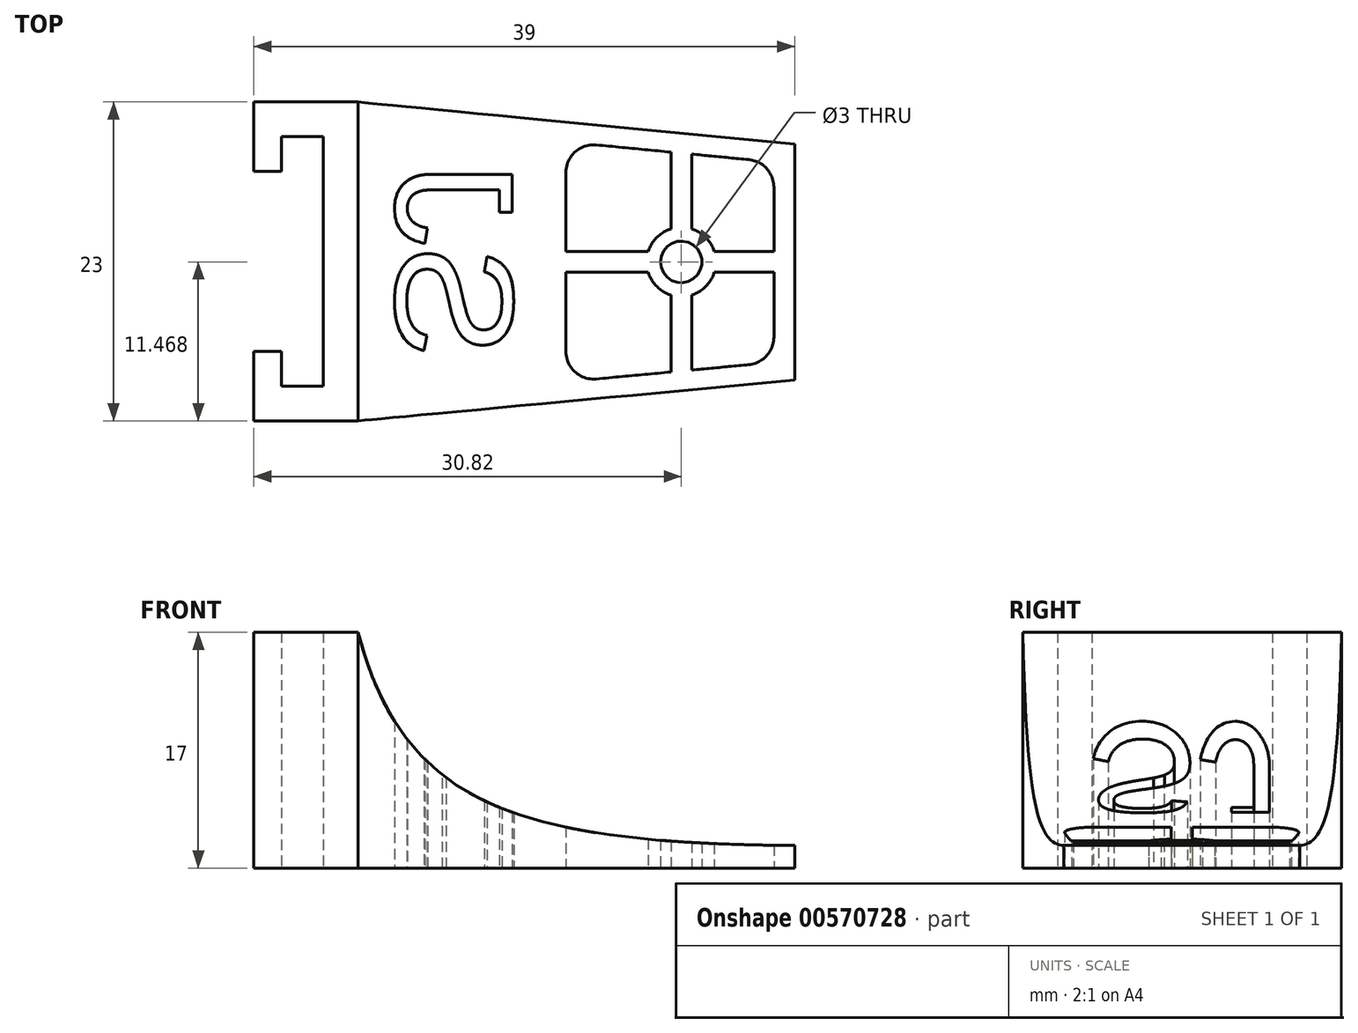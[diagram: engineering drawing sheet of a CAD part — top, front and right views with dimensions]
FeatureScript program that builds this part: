
annotation { "Feature Type Name" : "Feature", "Feature Type Description" : "" }
export const myFeature = defineFeature(function(context is Context, id is Id, definition is map)
    precondition{}
    {
        {
            var Q0;
            Q0=qCreatedBy(makeId("Top.planeOp"),FACE);
            var sketch = newSketch(context, id + "F0", { "sketchPlane" : qUnion([Q0])});
            skLineSegment(sketch, "E0.left", {"start": v(-1, -9) * mm, "end": v(-1, 9) * mm});
            skPoint(sketch, "E0.middle", {"position": v(0, 0) * mm});
            skLineSegment(sketch, "E1", {"start": v(-1, 9) * mm, "end": v(-4, 9) * mm});
            skLineSegment(sketch, "E2", {"start": v(-4, 9) * mm, "end": v(-4, 6.5) * mm});
            skLineSegment(sketch, "E3", {"start": v(-4, 6.5) * mm, "end": v(-6, 6.5) * mm});
            skLineSegment(sketch, "E4", {"start": v(-6, 6.5) * mm, "end": v(-6, 11.5) * mm});
            skLineSegment(sketch, "E5", {"start": v(-6, 11.5) * mm, "end": v(1.5, 11.5) * mm});
            skLineSegment(sketch, "E6.MirrorCS", {"start": v(-4, -9) * mm, "end": v(-4, -6.5) * mm});
            skLineSegment(sketch, "E7.MirrorCS", {"start": v(-4, -6.5) * mm, "end": v(-6, -6.5) * mm});
            skLineSegment(sketch, "E8.MirrorCS", {"start": v(-6, -6.5) * mm, "end": v(-6, -11.5) * mm});
            skLineSegment(sketch, "E9.MirrorCS", {"start": v(-1, -9) * mm, "end": v(-4, -9) * mm});
            skLineSegment(sketch, "E10.MirrorCS", {"start": v(-6, -11.5) * mm, "end": v(1.5, -11.5) * mm});
            skLineSegment(sketch, "E11", {"start": v(1.5, 11.5) * mm, "end": v(1.5, -11.5) * mm});
            skSolve(sketch);
        }
        {
            var Q0;
            Q0 = qSketchRegion(id + "F0", true);
            extrude(context, id + "F1", {"entities" : qUnion([Q0]), "depth" : 17 * mm, "offsetDistance" : 25 * mm});
        }
        {
            var Q0;
            Q0=makeQuery(id+"F1.opExtrude","CAP_FACE",FACE,{"disambiguationData":[OSD([sQuery(id+"F0.wireOp",EDGE,"E0.left"),sQuery(id+"F0.wireOp",EDGE,"E1"),sQuery(id+"F0.wireOp",EDGE,"E2"),sQuery(id+"F0.wireOp",EDGE,"E3"),sQuery(id+"F0.wireOp",EDGE,"E4"),sQuery(id+"F0.wireOp",EDGE,"E5"),sQuery(id+"F0.wireOp",EDGE,"E6.MirrorCS"),sQuery(id+"F0.wireOp",EDGE,"E7.MirrorCS"),sQuery(id+"F0.wireOp",EDGE,"E8.MirrorCS"),sQuery(id+"F0.wireOp",EDGE,"E9.MirrorCS"),sQuery(id+"F0.wireOp",EDGE,"E10.MirrorCS"),sQuery(id+"F0.wireOp",EDGE,"E11")])],"isStart":true});
            var sketch = newSketch(context, id + "F2", { "sketchPlane" : qUnion([Q0])});
            skLineSegment(sketch, "E12", {"start": v(15, 10.24) * mm, "end": v(15, -10.2) * mm});
            skLineSegment(sketch, "E13", {"start": v(1.5, 11.5) * mm, "end": v(33, 8.56) * mm});
            skLineSegment(sketch, "E14", {"start": v(33, 8.56) * mm, "end": v(33, -8.47) * mm});
            skLineSegment(sketch, "E15", {"start": v(33, -8.47) * mm, "end": v(1.5, -11.5) * mm});
            skLineSegment(sketch, "E16", {"start": v(33, 8.56) * mm, "end": v(15, -10.2) * mm, "construction": true});
            skLineSegment(sketch, "E17", {"start": v(33, -8.47) * mm, "end": v(15, 10.24) * mm, "construction": true});
            skCircle(sketch, "E18", {"center": v(24.82, 0.03) * mm, "radius": 2.5 * mm});
            skCircle(sketch, "E19", {"center": v(24.82, 0.03) * mm, "radius": 1.5 * mm});
            skLineSegment(sketch, "E20", {"start": v(24.82, 9.32) * mm, "end": v(24.82, -9.26) * mm, "construction": true});
            skLineSegment(sketch, "E21", {"start": v(33, 0.04) * mm, "end": v(15, 0.02) * mm, "construction": true});
            skLineSegment(sketch, "E22.bottom", {"start": v(16.5, 0.78) * mm, "end": v(22.44, 0.78) * mm});
            skLineSegment(sketch, "E22.top", {"start": v(16.5, -0.72) * mm, "end": v(22.44, -0.72) * mm});
            skLineSegment(sketch, "E23.left", {"start": v(24.07, 7.97) * mm, "end": v(24.07, 2.42) * mm});
            skLineSegment(sketch, "E23.right", {"start": v(25.57, 7.83) * mm, "end": v(25.57, 2.42) * mm});
            skPoint(sketch, "E22.right.start.orphan", {"position": v(36.55, 0.78) * mm});
            skPoint(sketch, "E24.orphan", {"position": v(36.55, -0.72) * mm});
            skPoint(sketch, "E23.top.end.orphan", {"position": v(25.57, -14.5) * mm});
            skPoint(sketch, "E25.orphan", {"position": v(24.07, -14.5) * mm});
            skPoint(sketch, "E23.bottom.end.orphan", {"position": v(25.57, 14.56) * mm});
            skPoint(sketch, "E26.orphan", {"position": v(24.07, 14.56) * mm});
            skLineSegment(sketch, "E27.trimOffspring", {"start": v(27.2, 0.78) * mm, "end": v(31.5, 0.78) * mm});
            skLineSegment(sketch, "E28.trimOffspring", {"start": v(27.2, -0.72) * mm, "end": v(31.5, -0.72) * mm});
            skLineSegment(sketch, "E29.trimOffspring", {"start": v(25.57, -0.72) * mm, "end": v(25.57, -0.75) * mm});
            skLineSegment(sketch, "E30.trimOffspring", {"start": v(25.57, 0.81) * mm, "end": v(25.57, 0.78) * mm});
            skLineSegment(sketch, "E31.trimOffspring", {"start": v(25.54, 0.78) * mm, "end": v(25.57, 0.78) * mm});
            skLineSegment(sketch, "E32.trimOffspring", {"start": v(25.57, -2.35) * mm, "end": v(25.57, -7.74) * mm});
            skLineSegment(sketch, "E33.trimOffspring", {"start": v(24.07, 0.81) * mm, "end": v(24.07, 0.78) * mm});
            skLineSegment(sketch, "E34.trimOffspring", {"start": v(24.07, 0.78) * mm, "end": v(24.1, 0.78) * mm});
            skLineSegment(sketch, "E35.trimOffspring", {"start": v(24.07, -0.72) * mm, "end": v(24.07, -0.75) * mm});
            skLineSegment(sketch, "E36.trimOffspring", {"start": v(25.54, -0.72) * mm, "end": v(25.57, -0.72) * mm});
            skLineSegment(sketch, "E37.trimOffspring", {"start": v(24.07, -2.35) * mm, "end": v(24.07, -7.89) * mm});
            skLineSegment(sketch, "E38.trimOffspring", {"start": v(24.07, -0.72) * mm, "end": v(24.1, -0.72) * mm});
            skPoint(sketch, "E22.left.start.orphan", {"position": v(13.1, 0.78) * mm});
            skPoint(sketch, "E39.orphan", {"position": v(13.1, -0.72) * mm});
            skText(sketch, "E40", { "text": "SJ", "fontName": "Arimo-Regular.ttf"});
            skLineSegment(sketch, "E41.left", {"start": v(16.5, 8.68) * mm, "end": v(16.5, -8.61) * mm});
            skLineSegment(sketch, "E42", {"start": v(31.5, 7.28) * mm, "end": v(31.5, -7.17) * mm});
            skLineSegment(sketch, "E43", {"start": v(16.5, 8.68) * mm, "end": v(31.5, 7.28) * mm});
            skLineSegment(sketch, "E44", {"start": v(16.5, -8.61) * mm, "end": v(31.5, -7.17) * mm});
            const initialGuessF2  = {"E40": [0.00426, 0.00698, 0, -1, 0.00874]};
            skSetInitialGuess(sketch, initialGuessF2);
            skSolve(sketch);
        }
        {
            var Q0;
            {var subQ2=sQuery(id+"F2.wireOp",EDGE,"E12");Q0=makeQuery(id+"F2.imprint","IMPRINT",FACE,{"disambiguationData":[TD([[makeQuery(id+"F2.imprint","IMPRINT",EDGE,{"derivedFrom":subQ2}),-1.0]])]});}
            var Q1;
            {var subQ8=sQuery(id+"F2.wireOp",EDGE,"E12");Q1=makeQuery(id+"F2.imprint","IMPRINT",FACE,{"disambiguationData":[TD([[makeQuery(id+"F2.imprint","IMPRINT",EDGE,{"derivedFrom":subQ8}),1.0]])]});}
            var Q2;
            {var subQ0=sQuery(id+"F2.wireOp",EDGE,"E22.bottom");Q2=makeQuery(id+"F2.imprint","IMPRINT",FACE,{"disambiguationData":[TD([[makeQuery(id+"F2.imprint","IMPRINT",EDGE,{"derivedFrom":subQ0}),-1.0]])]});}
            var Q3;
            {var subQ0=sQuery(id+"F2.wireOp",EDGE,"E32.trimOffspring");Q3=makeQuery(id+"F2.imprint","IMPRINT",FACE,{"disambiguationData":[TD([[makeQuery(id+"F2.imprint","IMPRINT",EDGE,{"derivedFrom":subQ0}),-1.0]])]});}
            var Q4;
            {var subQ0=sQuery(id+"F2.wireOp",EDGE,"E27.trimOffspring");Q4=makeQuery(id+"F2.imprint","IMPRINT",FACE,{"disambiguationData":[TD([[makeQuery(id+"F2.imprint","IMPRINT",EDGE,{"derivedFrom":subQ0}),-1.0]])]});}
            var Q5;
            {var subQ0=sQuery(id+"F2.wireOp",EDGE,"E23.left");Q5=makeQuery(id+"F2.imprint","IMPRINT",FACE,{"disambiguationData":[TD([[makeQuery(id+"F2.imprint","IMPRINT",EDGE,{"derivedFrom":subQ0}),1.0]])]});}
            var Q6;
            Q6=makeQuery(id+"F2.imprint","IMPRINT",FACE,{"disambiguationData":[TD([[makeQuery(id+"F2.imprint","IMPRINT",EDGE,{"derivedFrom":sQuery(id+"F2.wireOp",EDGE,"E19")}),-1.0]])]});
            extrude(context, id + "F3", {"entities" : qUnion([Q0, Q1, Q2, Q3, Q4, Q5, Q6]), "operationType" : NewBodyOperationType.ADD, "oppositeDirection" : true, "depth" : 17 * mm, "offsetDistance" : 25 * mm});
        }
        {
            var Q0;
            Q0=qCreatedBy(makeId("Front.planeOp"),FACE);
            var sketch = newSketch(context, id + "F4", { "sketchPlane" : qUnion([Q0])});
            skFitSpline(sketch, "E45", {"points": [v(33.1, 1.62) * mm, v(1.4, 17.42) * mm], "startDerivative": vector(-63.12, 0.42) * mm, "endDerivative": vector(-9.53, 37.5) * mm});
            skLineSegment(sketch, "E46", {"start": v(1.4, 17.42) * mm, "end": v(37.63, 20.99) * mm});
            skLineSegment(sketch, "E47", {"start": v(37.63, 20.99) * mm, "end": v(33.1, 1.62) * mm});
            skSolve(sketch);
        }
        {
            var Q0;
            Q0=makeQuery(id+"F4.imprint","IMPRINT",FACE,{"disambiguationData":[TD([[makeQuery(id+"F4.imprint","IMPRINT",EDGE,{"derivedFrom":sQuery(id+"F4.wireOp",EDGE,"E45")}),-1.0]])]});
            extrude(context, id + "F5", {"entities" : qUnion([Q0]), "operationType" : NewBodyOperationType.REMOVE, "oppositeDirection" : true, "depth" : 25 * mm, "offsetDistance" : 25 * mm, "hasSecondDirection" : true, "secondDirectionOppositeDirection" : false, "secondDirectionDepth" : 25 * mm});
        }
        {
            var Q0;
            Q0=makeQuery(id+"F3.opExtrude","SWEPT_EDGE",EDGE,{"disambiguationData":[OSD([sQuery(id+"F2.wireOp",EDGE,"E42"),sQuery(id+"F2.wireOp",EDGE,"E43")])]});
            var Q1;
            Q1=makeQuery(id+"F3.opExtrude","SWEPT_EDGE",EDGE,{"disambiguationData":[OSD([sQuery(id+"F2.wireOp",EDGE,"E42"),sQuery(id+"F2.wireOp",EDGE,"E44")])]});
            var Q2;
            Q2=makeQuery(id+"F3.opExtrude","SWEPT_EDGE",EDGE,{"disambiguationData":[OSD([sQuery(id+"F2.wireOp",EDGE,"E41.left"),sQuery(id+"F2.wireOp",EDGE,"E44")])]});
            var Q3;
            Q3=makeQuery(id+"F3.opExtrude","SWEPT_EDGE",EDGE,{"disambiguationData":[OSD([sQuery(id+"F2.wireOp",EDGE,"E41.left"),sQuery(id+"F2.wireOp",EDGE,"E43")])]});
            fillet(context, id + "F6", {"entities" : qUnion([Q0, Q1, Q2, Q3]), "radius" : 2 * mm, "tangentPropagation" : true, "allowEdgeOverflow" : false});
        }
    });
